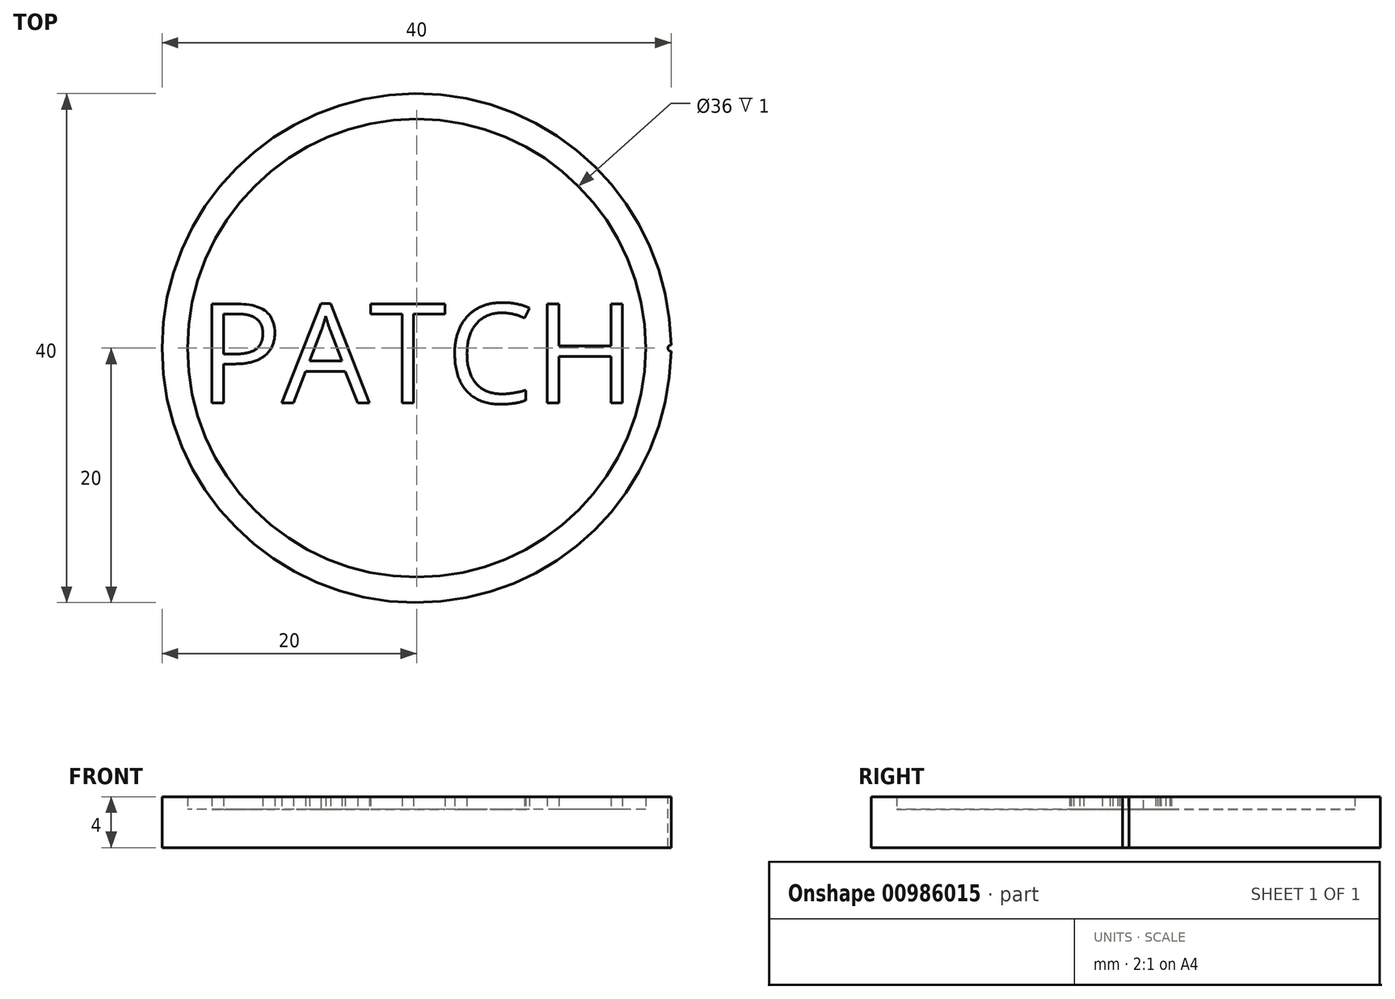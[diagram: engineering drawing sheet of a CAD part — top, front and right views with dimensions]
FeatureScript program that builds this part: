
annotation { "Feature Type Name" : "Feature", "Feature Type Description" : "" }
export const myFeature = defineFeature(function(context is Context, id is Id, definition is map)
    precondition{}
    {
        {
            var Q0;
            Q0=qCreatedBy(makeId("Top.planeOp"),FACE);
            var sketch = newSketch(context, id + "F0", { "sketchPlane" : qUnion([Q0])});
            skCircle(sketch, "E0", {"center": v(0, 0) * mm, "radius": 20 * mm});
            skSolve(sketch);
        }
        {
            var Q0;
            Q0=makeQuery(id+"F0.imprint","IMPRINT",FACE,{"disambiguationData":[TD([[makeQuery(id+"F0.imprint","IMPRINT",EDGE,{"derivedFrom":sQuery(id+"F0.wireOp",EDGE,"E0")}),1.0]])]});
            extrude(context, id + "F1", {"entities" : qUnion([Q0]), "depth" : 3 * mm, "offsetDistance" : 25 * mm});
        }
        {
            var Q0;
            Q0=makeQuery(id+"F1.opExtrude","CAP_FACE",FACE,{"disambiguationData":[OSD([sQuery(id+"F0.wireOp",EDGE,"E0")])],"isStart":false});
            var sketch = newSketch(context, id + "F2", { "sketchPlane" : qUnion([Q0])});
            skCircle(sketch, "E1", {"center": v(0, 0) * mm, "radius": 18 * mm});
            skSolve(sketch);
        }
        {
            var Q0;
            Q0=makeQuery(id+"F2.imprint","IMPRINT",FACE,{"disambiguationData":[TD([[makeQuery(id+"F2.imprint","IMPRINT",EDGE,{"derivedFrom":makeQuery(id+"F1.opExtrude","CAP_EDGE",EDGE,{"disambiguationData":[OSD([sQuery(id+"F0.wireOp",EDGE,"E0")])],"isStart":false})}),1.0]])]});
            extrude(context, id + "F3", {"entities" : qUnion([Q0]), "operationType" : NewBodyOperationType.ADD, "depth" : 1 * mm, "offsetDistance" : 25 * mm});
        }
        {
            var Q0;
            Q0=makeQuery(id+"F2.imprint","IMPRINT",FACE,{"disambiguationData":[TD([[makeQuery(id+"F2.imprint","IMPRINT",EDGE,{"derivedFrom":sQuery(id+"F2.wireOp",EDGE,"E1")}),1.0]])]});
            var sketch = newSketch(context, id + "F4", { "sketchPlane" : qUnion([Q0])});
            skText(sketch, "E2", { "text": "PATCH", "fontName": "OpenSans-Regular.ttf"});
            const initialGuessF4  = {"E2": [-0.01714, -0.0043, 1, 0, 0.00784]};
            skSetInitialGuess(sketch, initialGuessF4);
            skSolve(sketch);
        }
        {
            var Q0;
            Q0 = qSketchRegion(id + "F4", true);
            extrude(context, id + "F5", {"entities" : qUnion([Q0]), "operationType" : NewBodyOperationType.ADD, "depth" : 1 * mm, "offsetDistance" : 25 * mm});
        }
        {
            var Q0;
            Q0=makeQuery(id+"F3.opExtrude","CAP_FACE",FACE,{"disambiguationData":[OSD([sQuery(id+"F0.wireOp",EDGE,"E0"),sQuery(id+"F2.wireOp",EDGE,"E1")])],"isStart":false});
            var sketch = newSketch(context, id + "F6", { "sketchPlane" : qUnion([Q0])});
            skCircle(sketch, "E3", {"center": v(20, 0) * mm, "radius": 0.25 * mm});
            skSolve(sketch);
        }
        {
            var Q0;
            {var subQ0=sQuery(id+"F6.wireOp",EDGE,"E3");var subQ1=makeQuery(id+"F3.opExtrude","CAP_EDGE",EDGE,{"disambiguationData":[OSD([sQuery(id+"F0.wireOp",EDGE,"E0")])],"isStart":false});var subQ2=makeQuery(id+"F6.imprint","INTERSECT",VERTEX,{"disambiguationData":[OD(0.0)],"derivedFrom":[subQ1,subQ0]});Q0=makeQuery(id+"F6.imprint","IMPRINT",FACE,{"disambiguationData":[TD([[makeQuery(id+"F6.imprint","IMPRINT",EDGE,{"disambiguationData":[TD([[subQ2,1.0]])],"derivedFrom":subQ0}),1.0]])]});}
            var Q1;
            Q1=sQuery(id+"F6.wireOp",EDGE,"E3");
            extrude(context, id + "F7", {"entities" : qUnion([Q0]), "operationType" : NewBodyOperationType.REMOVE, "surfaceEntities" : qUnion([Q1]), "oppositeDirection" : true, "depth" : 25 * mm, "offsetDistance" : 25 * mm});
        }
        {
            var Q0;
            Q0=qCreatedBy(makeId("Front.planeOp"),FACE);
            var sketch = newSketch(context, id + "F8", { "sketchPlane" : qUnion([Q0])});
            skLineSegment(sketch, "E4", {"start": v(0, 0) * mm, "end": v(0, 3.71) * mm});
            skSolve(sketch);
        }
    });
